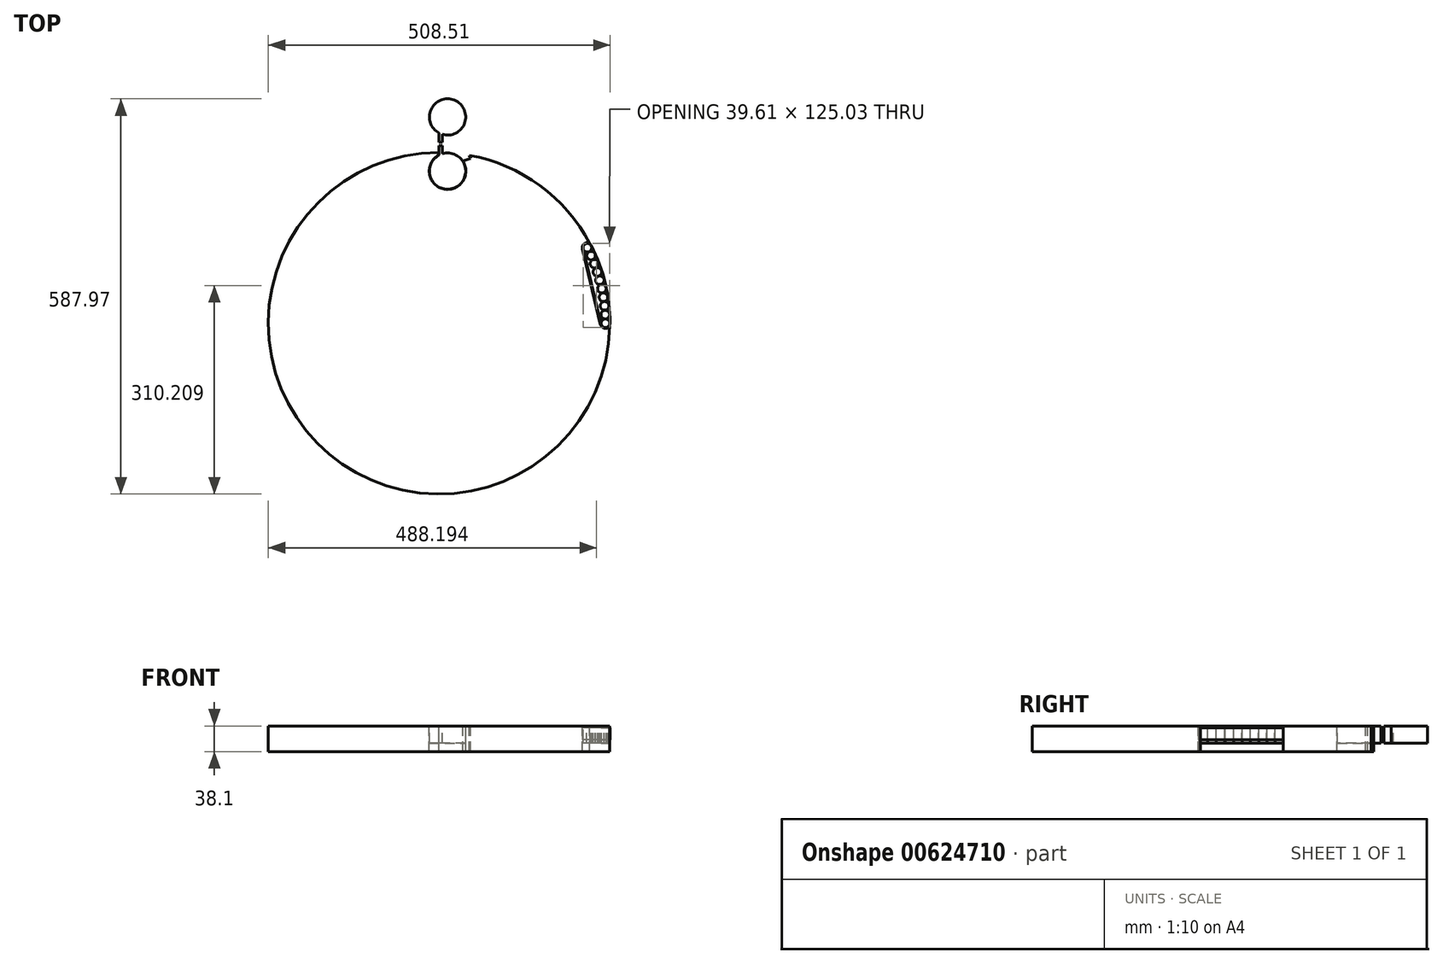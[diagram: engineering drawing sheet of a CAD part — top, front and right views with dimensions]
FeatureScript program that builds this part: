
annotation { "Feature Type Name" : "Feature", "Feature Type Description" : "" }
export const myFeature = defineFeature(function(context is Context, id is Id, definition is map)
    precondition{}
    {
        {
            var Q0;
            Q0=qCreatedBy(makeId("Top.planeOp"),FACE);
            var sketch = newSketch(context, id + "F0", { "sketchPlane" : qUnion([Q0])});
            skLineSegment(sketch, "E0.bottom", {"start": v(381, 381) * mm, "end": v(-381, 381) * mm});
            skLineSegment(sketch, "E0.top", {"start": v(381, -381) * mm, "end": v(-381, -381) * mm});
            skLineSegment(sketch, "E0.left", {"start": v(381, 381) * mm, "end": v(381, -381) * mm});
            skLineSegment(sketch, "E0.right", {"start": v(-381, 381) * mm, "end": v(-381, -381) * mm});
            skSolve(sketch);
        }
        {
            var Q0;
            Q0=makeQuery(id+"F0.imprint","IMPRINT",FACE,{"disambiguationData":[TD([[makeQuery(id+"F0.imprint","IMPRINT",EDGE,{"derivedFrom":sQuery(id+"F0.wireOp",EDGE,"E0.bottom")}),1.0]])]});
            extrude(context, id + "F1", {"entities" : qUnion([Q0]), "oppositeDirection" : true, "depth" : 38.1 * mm, "offsetDistance" : 25.4 * mm});
        }
        {
            var Q0;
            Q0=makeQuery(id+"F1.opExtrude","CAP_FACE",FACE,{"disambiguationData":[OSD([sQuery(id+"F0.wireOp",EDGE,"E0.bottom"),sQuery(id+"F0.wireOp",EDGE,"E0.top"),sQuery(id+"F0.wireOp",EDGE,"E0.left"),sQuery(id+"F0.wireOp",EDGE,"E0.right")])],"isStart":true});
            var sketch = newSketch(context, id + "F2", { "sketchPlane" : qUnion([Q0])});
            skCircle(sketch, "E1", {"center": v(0, 0) * mm, "radius": 254 * mm});
            skCircle(sketch, "E2", {"center": v(0, 0) * mm, "radius": 279.4 * mm});
            skCircle(sketch, "E3", {"center": v(247.65, 0) * mm, "radius": 6.35 * mm, "construction": true});
            skCircle(sketch, "E4.1.0", {"center": v(247.31, 12.95) * mm, "radius": 6.35 * mm, "construction": true});
            skCircle(sketch, "E4.2.0", {"center": v(246.3, 25.87) * mm, "radius": 6.35 * mm, "construction": true});
            skCircle(sketch, "E4.3.0", {"center": v(244.6, 38.72) * mm, "radius": 6.35 * mm, "construction": true});
            skCircle(sketch, "E4.4.0", {"center": v(242.24, 51.46) * mm, "radius": 6.35 * mm, "construction": true});
            skCircle(sketch, "E4.5.0", {"center": v(239.22, 64.06) * mm, "radius": 6.35 * mm, "construction": true});
            skCircle(sketch, "E4.6.0", {"center": v(235.54, 76.49) * mm, "radius": 6.35 * mm, "construction": true});
            skCircle(sketch, "E4.7.0", {"center": v(231.22, 88.7) * mm, "radius": 6.35 * mm, "construction": true});
            skCircle(sketch, "E4.8.0", {"center": v(226.26, 100.68) * mm, "radius": 6.35 * mm, "construction": true});
            skCircle(sketch, "E4.9.0", {"center": v(220.69, 112.37) * mm, "radius": 6.35 * mm, "construction": true});
            skLineSegment(sketch, "E4.anchor1", {"start": v(0, 0) * mm, "end": v(247.65, 0) * mm, "construction": true});
            skLineSegment(sketch, "E4.anchor2", {"start": v(0, 0) * mm, "end": v(220.69, 112.37) * mm, "construction": true});
            skLineSegment(sketch, "E5.bottom", {"start": v(381, 381) * mm, "end": v(-381, 381) * mm});
            skLineSegment(sketch, "E5.top", {"start": v(381, -381) * mm, "end": v(-381, -381) * mm});
            skLineSegment(sketch, "E5.left", {"start": v(381, 381) * mm, "end": v(381, -381) * mm});
            skLineSegment(sketch, "E5.right", {"start": v(-381, 381) * mm, "end": v(-381, -381) * mm});
            skCircle(sketch, "E6.0", {"center": v(247.65, 0) * mm, "radius": 7.62 * mm, "construction": true});
            skCircle(sketch, "E7.0", {"center": v(220.69, 112.37) * mm, "radius": 7.62 * mm, "construction": true});
            skLineSegment(sketch, "E8", {"start": v(213.28, 110.6) * mm, "end": v(240.24, -1.78) * mm, "construction": true});
            skArc(sketch, "E9", {"start": v(213.28, 110.6) * mm, "mid": v(216.07, 118.44) * mm, "end": v(224.38, 119.04) * mm});
            skArc(sketch, "E10", {"start": v(240.24, -1.78) * mm, "mid": v(246.3, -7.5) * mm, "end": v(253.96, -4.27) * mm});
            skLineSegment(sketch, "E11", {"start": v(241.48, -1.48) * mm, "end": v(214.51, 110.9) * mm, "construction": true});
            skArc(sketch, "E12", {"start": v(226.35, 115.26) * mm, "mid": v(246.99, 59.26) * mm, "end": v(254, 0) * mm, "construction": true});
            skArc(sketch, "E13", {"start": v(241.48, -1.48) * mm, "mid": v(248.4, -6.3) * mm, "end": v(254, 0) * mm});
            skArc(sketch, "E14", {"start": v(214.51, 110.9) * mm, "mid": v(218.49, 118.33) * mm, "end": v(226.35, 115.26) * mm, "construction": true});
            skSolve(sketch);
        }
        {
            var Q0;
            Q0=makeQuery(id+"F2.imprint","IMPRINT",FACE,{"disambiguationData":[TD([[makeQuery(id+"F2.imprint","IMPRINT",EDGE,{"derivedFrom":sQuery(id+"F2.wireOp",EDGE,"E2")}),1.0]])]});
            var Q1;
            Q1=makeQuery(id+"F2.imprint","IMPRINT",FACE,{"disambiguationData":[TD([[makeQuery(id+"F2.imprint","IMPRINT",EDGE,{"derivedFrom":sQuery(id+"F2.wireOp",EDGE,"E8")}),1.0]])]});
            extrude(context, id + "F3", {"entities" : qUnion([Q0, Q1]), "operationType" : NewBodyOperationType.REMOVE, "endBound" : BoundingType.THROUGH_ALL, "oppositeDirection" : true, "depth" : 50.8 * mm, "offsetDistance" : 25.4 * mm});
        }
        {
            var Q0;
            Q0=makeQuery(id+"F0.imprint","IMPRINT",FACE,{"disambiguationData":[TD([[makeQuery(id+"F0.imprint","IMPRINT",EDGE,{"derivedFrom":sQuery(id+"F0.wireOp",EDGE,"E0.bottom")}),1.0]])]});
            var sketch = newSketch(context, id + "F4", { "sketchPlane" : qUnion([Q0])});
            skLineSegment(sketch, "E15.0", {"start": v(213.28, 110.6) * mm, "end": v(240.24, -1.78) * mm});
            skArc(sketch, "E15.1", {"start": v(213.28, 110.6) * mm, "mid": v(216.07, 118.44) * mm, "end": v(224.38, 119.04) * mm});
            skArc(sketch, "E15.3", {"start": v(240.24, -1.78) * mm, "mid": v(246.3, -7.5) * mm, "end": v(253.96, -4.27) * mm});
            skArc(sketch, "E16", {"start": v(224.38, 119.04) * mm, "mid": v(246.99, 59.26) * mm, "end": v(253.96, -4.27) * mm});
            skSolve(sketch);
        }
        {
            var Q0;
            Q0 = qSketchRegion(id + "F4", true);
            extrude(context, id + "F5", {"entities" : qUnion([Q0]), "operationType" : NewBodyOperationType.REMOVE, "endBound" : BoundingType.THROUGH_ALL, "oppositeDirection" : true, "depth" : 50.8 * mm, "offsetDistance" : 25.4 * mm});
        }
        {
            var Q0;
            Q0=makeQuery(id+"F2.imprint","IMPRINT",FACE,{"disambiguationData":[TD([[makeQuery(id+"F2.imprint","IMPRINT",EDGE,{"derivedFrom":sQuery(id+"F2.wireOp",EDGE,"E2")}),1.0]])]});
            var sketch = newSketch(context, id + "F6", { "sketchPlane" : qUnion([Q0])});
            skLineSegment(sketch, "E17.0", {"start": v(241.48, -1.48) * mm, "end": v(214.51, 110.9) * mm});
            skArc(sketch, "E18.0", {"start": v(214.51, 110.9) * mm, "mid": v(218.49, 118.33) * mm, "end": v(226.35, 115.26) * mm});
            skArc(sketch, "E19.0", {"start": v(226.35, 115.26) * mm, "mid": v(246.99, 59.26) * mm, "end": v(254, 0) * mm});
            skArc(sketch, "E20.0", {"start": v(241.48, -1.48) * mm, "mid": v(248.4, -6.3) * mm, "end": v(254, 0) * mm});
            skLineSegment(sketch, "E21.0", {"start": v(240.98, -1.6) * mm, "end": v(214.02, 110.77) * mm});
            skArc(sketch, "E21.1", {"start": v(240.98, -1.6) * mm, "mid": v(248.46, -6.81) * mm, "end": v(254.5, 0) * mm});
            skArc(sketch, "E21.2", {"start": v(226.8, 115.49) * mm, "mid": v(247.48, 59.38) * mm, "end": v(254.5, 0) * mm});
            skArc(sketch, "E21.3", {"start": v(214.02, 110.77) * mm, "mid": v(218.31, 118.8) * mm, "end": v(226.8, 115.49) * mm});
            skSolve(sketch);
        }
        {
            var Q0;
            Q0 = qSketchRegion(id + "F6", true);
            extrude(context, id + "F7", {"entities" : qUnion([Q0]), "oppositeDirection" : true, "depth" : 20.32 * mm, "offsetDistance" : 25.4 * mm, "hasSecondDirection" : true, "secondDirectionOppositeDirection" : true, "secondDirectionDepth" : 2.54 * mm});
        }
        {
            var Q0;
            Q0=makeQuery(id+"F0.imprint","IMPRINT",FACE,{"disambiguationData":[TD([[makeQuery(id+"F0.imprint","IMPRINT",EDGE,{"derivedFrom":sQuery(id+"F0.wireOp",EDGE,"E0.bottom")}),1.0]])]});
            var sketch = newSketch(context, id + "F8", { "sketchPlane" : qUnion([Q0])});
            skCircle(sketch, "E22.0", {"center": v(247.65, 0) * mm, "radius": 6.35 * mm});
            skCircle(sketch, "E22.1", {"center": v(247.31, 12.95) * mm, "radius": 6.35 * mm});
            skCircle(sketch, "E22.2", {"center": v(246.3, 25.87) * mm, "radius": 6.35 * mm});
            skCircle(sketch, "E22.3", {"center": v(244.6, 38.72) * mm, "radius": 6.35 * mm});
            skCircle(sketch, "E22.4", {"center": v(242.24, 51.46) * mm, "radius": 6.35 * mm});
            skCircle(sketch, "E22.5", {"center": v(239.22, 64.06) * mm, "radius": 6.35 * mm});
            skCircle(sketch, "E22.6", {"center": v(235.54, 76.49) * mm, "radius": 6.35 * mm});
            skCircle(sketch, "E22.7", {"center": v(231.22, 88.7) * mm, "radius": 6.35 * mm});
            skCircle(sketch, "E22.8", {"center": v(226.26, 100.68) * mm, "radius": 6.35 * mm});
            skCircle(sketch, "E22.9", {"center": v(220.69, 112.37) * mm, "radius": 6.35 * mm});
            skSolve(sketch);
        }
        {
            var Q0;
            Q0 = qSketchRegion(id + "F8", true);
            extrude(context, id + "F9", {"entities" : qUnion([Q0]), "oppositeDirection" : true, "depth" : 25.4 * mm, "offsetDistance" : 25.4 * mm});
        }
        {
            var Q0;
            {var subQ0=sQuery(id+"F0.wireOp",EDGE,"E0.left");var subQ1=sQuery(id+"F0.wireOp",EDGE,"E0.top");var subQ2=sQuery(id+"F0.wireOp",EDGE,"E0.right");var subQ3=sQuery(id+"F0.wireOp",EDGE,"E0.bottom");Q0=makeQuery(id+"F3.boolean.opBoolean","SPLIT",FACE,{"disambiguationData":[TD([makeQuery(id+"F1.opExtrude","SWEPT_FACE",FACE,{"disambiguationData":[OSD([subQ3])]})])],"derivedFrom":makeQuery(id+"F1.opExtrude","CAP_FACE",FACE,{"disambiguationData":[OSD([subQ3,subQ1,subQ0,subQ2])],"isStart":true})});}
            var sketch = newSketch(context, id + "F10", { "sketchPlane" : qUnion([Q0])});
            skLineSegment(sketch, "E23", {"start": v(0, 264.51) * mm, "end": v(0, 226.41) * mm});
            skCircle(sketch, "E24", {"center": v(12.7, 226.41) * mm, "radius": 12.7 * mm});
            skLineSegment(sketch, "E25", {"start": v(0, 254) * mm, "end": v(0, 279.4) * mm, "construction": true});
            skLineSegment(sketch, "E26", {"start": v(-17.01, 266.7) * mm, "end": v(17.01, 266.7) * mm, "construction": true});
            skPoint(sketch, "E26.startSnap0", {"position": v(0, 266.7) * mm});
            skLineSegment(sketch, "E27", {"start": v(8.9, 238.53) * mm, "end": v(45.25, 249.94) * mm});
            skLineSegment(sketch, "E28", {"start": v(45.25, 249.94) * mm, "end": v(46.77, 245.09) * mm});
            skLineSegment(sketch, "E29", {"start": v(46.77, 245.09) * mm, "end": v(34.16, 241.13) * mm});
            skArc(sketch, "E30", {"start": v(34.16, 241.13) * mm, "mid": v(27.36, 236) * mm, "end": v(25.33, 227.71) * mm});
            skLineSegment(sketch, "E31.1.0", {"start": v(5.08, 264.51) * mm, "end": v(5.08, 251.3) * mm});
            skArc(sketch, "E31.1.1", {"start": v(5.08, 251.3) * mm, "mid": v(7.94, 243.27) * mm, "end": v(15.24, 238.86) * mm});
            skLineSegment(sketch, "E31.1.2", {"start": v(0, 264.51) * mm, "end": v(5.08, 264.51) * mm});
            skLineSegment(sketch, "E31.anchor1", {"start": v(12.7, 226.41) * mm, "end": v(25.33, 227.71) * mm, "construction": true});
            skLineSegment(sketch, "E31.anchor2", {"start": v(12.7, 226.41) * mm, "end": v(15.24, 238.86) * mm, "construction": true});
            skArc(sketch, "E32", {"start": v(45.25, 249.94) * mm, "mid": v(25.01, 264.64) * mm, "end": v(0, 264.51) * mm});
            skLineSegment(sketch, "E33.MirrorCS", {"start": v(0, 268.89) * mm, "end": v(0, 306.99) * mm});
            skCircle(sketch, "E34.MirrorC", {"center": v(12.7, 306.99) * mm, "radius": 12.7 * mm});
            skArc(sketch, "E35.MirrorCS", {"start": v(34.16, 292.27) * mm, "mid": v(27.36, 297.4) * mm, "end": v(25.33, 305.69) * mm});
            skLineSegment(sketch, "E36.MirrorCS", {"start": v(45.25, 283.46) * mm, "end": v(46.77, 288.31) * mm});
            skLineSegment(sketch, "E37.MirrorCS", {"start": v(46.77, 288.31) * mm, "end": v(34.16, 292.27) * mm});
            skArc(sketch, "E38.MirrorCS", {"start": v(45.25, 283.46) * mm, "mid": v(25.01, 268.76) * mm, "end": v(0, 268.89) * mm});
            skCircle(sketch, "E39", {"center": v(12.7, 226.41) * mm, "radius": 27.23 * mm, "construction": true});
            skLineSegment(sketch, "E40", {"start": v(12.7, 226.41) * mm, "end": v(14.23, 253.6) * mm, "construction": true});
            skArc(sketch, "E41", {"start": v(0, 250.5) * mm, "mid": v(5.99, 200.02) * mm, "end": v(35.36, 241.51) * mm});
            skSolve(sketch);
        }
        {
            var Q0;
            Q0 = qSketchRegion(id + "F10", true);
            var Q1;
            {var subQ0=sQuery(id+"F10.wireOp",EDGE,"E27");var subQ1=sQuery(id+"F10.wireOp",EDGE,"E24");var subQ2=makeQuery(id+"F10.imprint","INTERSECT",VERTEX,{"derivedFrom":[subQ1,subQ0]});Q1=makeQuery(id+"F10.imprint","IMPRINT",FACE,{"disambiguationData":[TD([[makeQuery(id+"F10.imprint","IMPRINT",EDGE,{"disambiguationData":[TD([[subQ2,1.0]])],"derivedFrom":subQ1}),-1.0]])]});}
            var Q2;
            {var subQ0=sQuery(id+"F10.wireOp",EDGE,"E24");var subQ1=makeQuery(id+"F10.imprint","INTERSECT",VERTEX,{"derivedFrom":[subQ0,sQuery(id+"F10.wireOp",EDGE,"E27")]});Q2=makeQuery(id+"F10.imprint","IMPRINT",FACE,{"disambiguationData":[TD([[makeQuery(id+"F10.imprint","IMPRINT",EDGE,{"disambiguationData":[TD([[subQ1,1.0]])],"derivedFrom":subQ0}),1.0]])]});}
            extrude(context, id + "F11", {"entities" : qUnion([Q0, Q1, Q2]), "operationType" : NewBodyOperationType.REMOVE, "endBound" : BoundingType.UP_TO_NEXT, "oppositeDirection" : true, "depth" : 25.4 * mm, "offsetDistance" : 25.4 * mm});
        }
        {
            var Q0;
            {var subQ0=sQuery(id+"F10.wireOp",EDGE,"E34.MirrorC");var subQ1=makeQuery(id+"F10.imprint","INTERSECT",VERTEX,{"derivedFrom":[sQuery(id+"F10.wireOp",EDGE,"E33.MirrorCS"),subQ0]});Q0=makeQuery(id+"F10.imprint","IMPRINT",FACE,{"disambiguationData":[TD([[makeQuery(id+"F10.imprint","IMPRINT",EDGE,{"disambiguationData":[TD([[subQ1,-1.0]])],"derivedFrom":subQ0}),-1.0]])]});}
            var Q1;
            {var subQ1=sQuery(id+"F10.wireOp",EDGE,"E35.MirrorCS");Q1=makeQuery(id+"F10.imprint","IMPRINT",FACE,{"disambiguationData":[TD([[makeQuery(id+"F10.imprint","IMPRINT",EDGE,{"derivedFrom":subQ1}),1.0]])]});}
            extrude(context, id + "F12", {"entities" : qUnion([Q0, Q1]), "operationType" : NewBodyOperationType.REMOVE, "endBound" : BoundingType.UP_TO_NEXT, "oppositeDirection" : true, "depth" : 25.4 * mm, "offsetDistance" : 25.4 * mm});
        }
        {
            var Q0;
            {var subQ1=sQuery(id+"F10.wireOp",EDGE,"E23");Q0=makeQuery(id+"F10.imprint","IMPRINT",FACE,{"disambiguationData":[TD([[makeQuery(id+"F10.imprint","IMPRINT",EDGE,{"derivedFrom":subQ1}),-1.0]])]});}
            var sketch = newSketch(context, id + "F13", { "sketchPlane" : qUnion([Q0])});
            skArc(sketch, "E42.0.0", {"start": v(25.33, 227.71) * mm, "mid": v(22.11, 234.94) * mm, "end": v(15.24, 238.86) * mm, "construction": true});
            skArc(sketch, "E42.0.3", {"start": v(0, 226.41) * mm, "mid": v(13.35, 213.73) * mm, "end": v(25.33, 227.71) * mm, "construction": true});
            skArc(sketch, "E43.0.2", {"start": v(12.62, 239.7) * mm, "mid": v(7.13, 244.38) * mm, "end": v(5.08, 251.3) * mm, "construction": true});
            skLineSegment(sketch, "E43.0.3", {"start": v(5.08, 251.3) * mm, "end": v(5.08, 264.51) * mm, "construction": true});
            skLineSegment(sketch, "E43.0.4", {"start": v(5.08, 264.51) * mm, "end": v(0, 264.51) * mm, "construction": true});
            skLineSegment(sketch, "E43.0.5", {"start": v(0, 264.51) * mm, "end": v(0, 226.41) * mm, "construction": true});
            skArc(sketch, "E44.0.1", {"start": v(15.24, 238.86) * mm, "mid": v(13.9, 239.2) * mm, "end": v(12.62, 239.7) * mm, "construction": true});
            skLineSegment(sketch, "E45.0", {"start": v(4.83, 264.26) * mm, "end": v(0.25, 264.26) * mm});
            skLineSegment(sketch, "E45.1", {"start": v(4.83, 251.3) * mm, "end": v(4.83, 264.26) * mm});
            skArc(sketch, "E45.2", {"start": v(0.25, 226.41) * mm, "mid": v(13.34, 213.98) * mm, "end": v(25.08, 227.69) * mm});
            skArc(sketch, "E45.3", {"start": v(25.08, 227.69) * mm, "mid": v(21.92, 234.77) * mm, "end": v(15.19, 238.6) * mm});
            skArc(sketch, "E45.4", {"start": v(15.19, 238.6) * mm, "mid": v(13.83, 238.96) * mm, "end": v(12.51, 239.46) * mm});
            skLineSegment(sketch, "E45.5", {"start": v(0.25, 264.26) * mm, "end": v(0.25, 226.41) * mm});
            skArc(sketch, "E45.6", {"start": v(12.51, 239.46) * mm, "mid": v(6.92, 244.24) * mm, "end": v(4.83, 251.3) * mm});
            skLineSegment(sketch, "E46.0", {"start": v(-17.01, 266.7) * mm, "end": v(17.01, 266.7) * mm, "construction": true});
            skLineSegment(sketch, "E47.MirrorCS", {"start": v(4.83, 282.1) * mm, "end": v(4.83, 269.14) * mm});
            skLineSegment(sketch, "E48.MirrorCS", {"start": v(0.25, 269.14) * mm, "end": v(0.25, 306.99) * mm});
            skLineSegment(sketch, "E49.MirrorCS", {"start": v(4.83, 269.14) * mm, "end": v(0.25, 269.14) * mm});
            skArc(sketch, "E50.MirrorCS", {"start": v(0.25, 306.99) * mm, "mid": v(13.34, 319.42) * mm, "end": v(25.08, 305.71) * mm});
            skArc(sketch, "E51.MirrorCS", {"start": v(25.08, 305.71) * mm, "mid": v(21.92, 298.63) * mm, "end": v(15.19, 294.8) * mm});
            skArc(sketch, "E52.MirrorCS", {"start": v(15.19, 294.8) * mm, "mid": v(13.83, 294.44) * mm, "end": v(12.51, 293.94) * mm});
            skArc(sketch, "E53.MirrorCS", {"start": v(12.51, 293.94) * mm, "mid": v(6.92, 289.16) * mm, "end": v(4.83, 282.1) * mm});
            skArc(sketch, "E54.0", {"start": v(0, 250.5) * mm, "mid": v(5.99, 200.02) * mm, "end": v(35.36, 241.51) * mm});
            skCircle(sketch, "E55.0", {"center": v(12.7, 226.41) * mm, "radius": 27.23 * mm, "construction": true});
            skCircle(sketch, "E56.0", {"center": v(12.7, 226.41) * mm, "radius": 26.98 * mm});
            skArc(sketch, "E57", {"start": v(4.83, 254) * mm, "mid": v(5.34, 252.93) * mm, "end": v(6.5, 252.67) * mm});
            skLineSegment(sketch, "E58", {"start": v(6.5, 252.67) * mm, "end": v(6.5, 252.67) * mm});
            skSolve(sketch);
        }
        {
            var Q0;
            Q0=makeQuery(id+"F13.imprint","IMPRINT",FACE,{"disambiguationData":[TD([[makeQuery(id+"F13.imprint","IMPRINT",EDGE,{"derivedFrom":sQuery(id+"F13.wireOp",EDGE,"E45.0")}),1.0]])]});
            var Q1;
            {var subQ0=sQuery(id+"F13.wireOp",EDGE,"E45.2");Q1=makeQuery(id+"F13.imprint","IMPRINT",FACE,{"disambiguationData":[TD([[makeQuery(id+"F13.imprint","IMPRINT",EDGE,{"derivedFrom":subQ0}),1.0]])]});}
            var Q2;
            {var subQ3=sQuery(id+"F10.wireOp",EDGE,"E30");var subQ9=makeQuery(id+"F10.imprint","IMPRINT",EDGE,{"derivedFrom":subQ3});Q2=makeQuery(id+"F13.imprint","IMPRINT",FACE,{"disambiguationData":[TD([[makeQuery(id+"F13.imprint","IMPRINT",EDGE,{"derivedFrom":subQ9}),1.0]])]});}
            var Q3;
            {var subQ18=sQuery(id+"F13.wireOp",EDGE,"E45.2");Q3=makeQuery(id+"F13.imprint","IMPRINT",FACE,{"disambiguationData":[TD([[makeQuery(id+"F13.imprint","IMPRINT",EDGE,{"derivedFrom":subQ18}),-1.0]])]});}
            extrude(context, id + "F14", {"entities" : qUnion([Q0, Q1, Q2, Q3]), "oppositeDirection" : true, "depth" : 25.4 * mm, "offsetDistance" : 25.4 * mm});
        }
        {
            var Q0;
            Q0=sQuery(id+"F10.wireOp",EDGE,"E25");
            cPlane(context, id + "F15", {"entities" : qUnion([Q0]), "cplaneType" : CPlaneType.MID_PLANE, "offset" : 25.4 * mm, "width" : 152.4 * mm, "height" : 152.4 * mm});
        }
        {
            var Q0;
            Q0=makeQuery(id+"F14.opExtrude","SWEPT_BODY",BODY,{"disambiguationData":[OSD([sQuery(id+"F13.wireOp",EDGE,"E45.0"),sQuery(id+"F13.wireOp",EDGE,"E45.1"),sQuery(id+"F13.wireOp",EDGE,"E45.2"),sQuery(id+"F13.wireOp",EDGE,"E45.3"),sQuery(id+"F13.wireOp",EDGE,"E45.4"),sQuery(id+"F13.wireOp",EDGE,"E45.5"),sQuery(id+"F13.wireOp",EDGE,"E45.6")])]});
            var Q1;
            Q1=qCreatedBy(id+"F15.planeOp",FACE);
            mirror(context, id + "F16", {"entities" : qUnion([Q0]), "mirrorPlane" : qUnion([Q1])});
        }
    });
